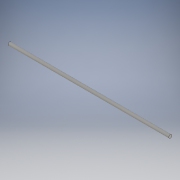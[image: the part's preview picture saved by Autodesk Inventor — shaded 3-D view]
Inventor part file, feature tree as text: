
AUTODESK INVENTOR PART (.ipt)
format: ipt  version: 2018 (Build 220112000, 112)  size: 93,184 bytes
history: native  units: in
note: dims shown in document units (in); Inventor stores cm internally (conversion verified against a paired STEP export)
features: revolve x1, thread x1, sketch x1
ambient origin geometry x8: Origin, YZ Plane, XZ Plane, XY Plane, X Axis, Y Axis, Z Axis, Center Point
bodies: Solid1 (feature_tree)
feature tree (3):
  revolve  "Revolution1"  [1 undecoded]
  thread  "Thread1"  [1 undecoded]
  sketch  "Sketch1"  dims[d0=0.1575in d1=15.748in d2=90.0deg d3=0.3937in d4=0.0in]
note: 2 required parameter values undecoded (feature->parameter linkage not recoverable at this tier; creation-order binding heuristic only, values carry confidence <= 0.55)